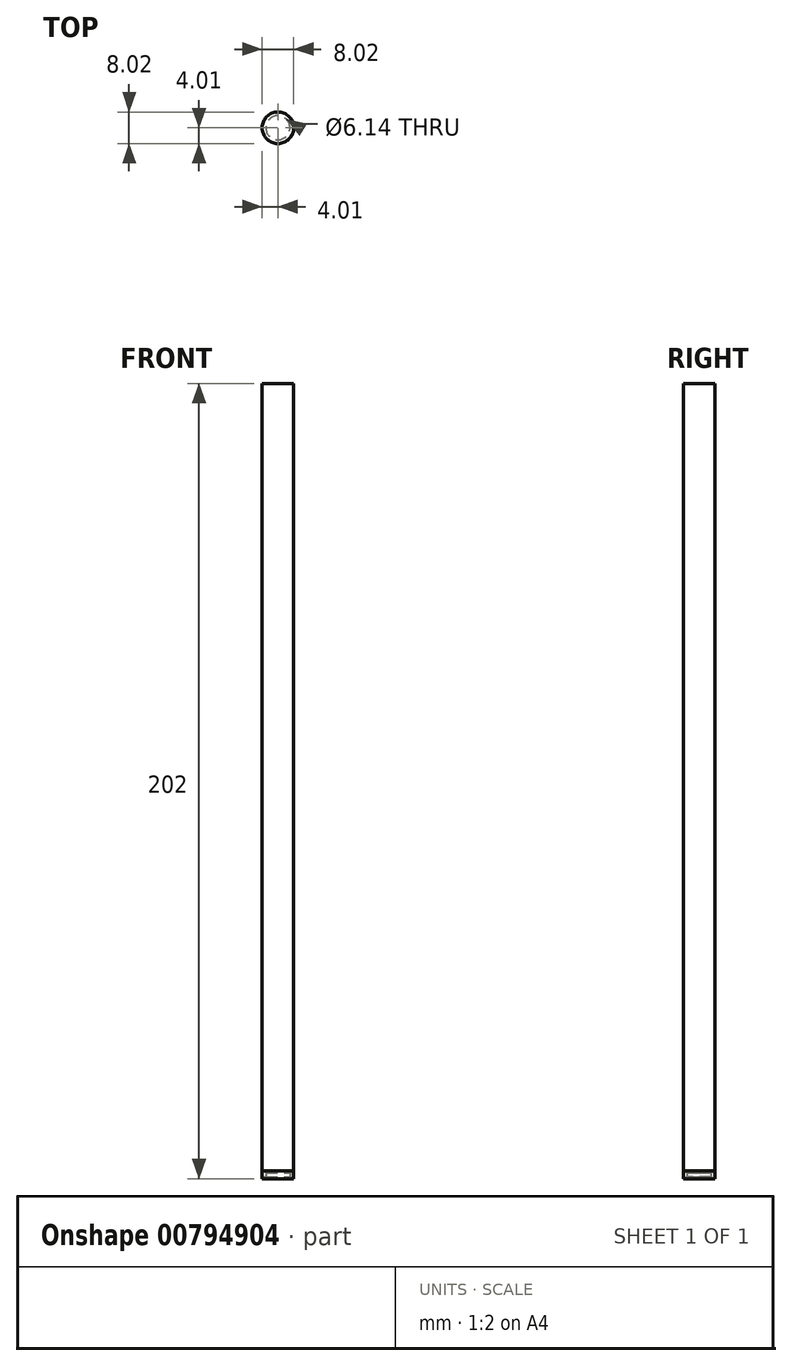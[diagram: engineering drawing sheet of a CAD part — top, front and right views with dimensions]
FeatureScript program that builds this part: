
annotation { "Feature Type Name" : "Feature", "Feature Type Description" : "" }
export const myFeature = defineFeature(function(context is Context, id is Id, definition is map)
    precondition{}
    {
        {
            var Q0;
            Q0=qCreatedBy(makeId("Top.planeOp"),FACE);
            var sketch = newSketch(context, id + "F0", { "sketchPlane" : qUnion([Q0])});
            skCircle(sketch, "E0", {"center": v(0, 0) * mm, "radius": 4 * mm});
            skSolve(sketch);
        }
        {
            var Q0;
            Q0=makeQuery(id+"F0.imprint","IMPRINT",FACE,{"disambiguationData":[TD([[makeQuery(id+"F0.imprint","IMPRINT",EDGE,{"derivedFrom":sQuery(id+"F0.wireOp",EDGE,"E0")}),1.0]])]});
            extrude(context, id + "F1", {"entities" : qUnion([Q0]), "depth" : 200 * mm, "offsetDistance" : 25.4 * mm});
        }
        {
            var Q0;
            Q0=qCreatedBy(makeId("Right.planeOp"),FACE);
            var sketch = newSketch(context, id + "F2", { "sketchPlane" : qUnion([Q0])});
            skLineSegment(sketch, "E1", {"start": v(-4.01, 0) * mm, "end": v(-3.07, -0.5) * mm});
            skLineSegment(sketch, "E2", {"start": v(-3.07, -0.5) * mm, "end": v(-3.07, -1.5) * mm});
            skLineSegment(sketch, "E3", {"start": v(-3.07, -1.5) * mm, "end": v(-4.01, -2) * mm});
            skLineSegment(sketch, "E4", {"start": v(-4.01, -2) * mm, "end": v(-4.01, 0) * mm});
            skSolve(sketch);
        }
        {
            var Q0;
            Q0=makeQuery(id+"F2.imprint","IMPRINT",FACE,{"disambiguationData":[TD([[makeQuery(id+"F2.imprint","IMPRINT",EDGE,{"derivedFrom":sQuery(id+"F2.wireOp",EDGE,"E1")}),-1.0]])]});
            var Q1;
            Q1=makeQuery(id+"F1.opExtrude","CAP_EDGE",EDGE,{"disambiguationData":[OSD([sQuery(id+"F0.wireOp",EDGE,"E0")])],"isStart":true});
            revolve(context, id + "F3", {"surfaceOperationType" : NewSurfaceOperationType.NEW, "entities" : qUnion([Q0]), "axis" : qUnion([Q1]), "revolveType" : RevolveType.FULL});
        }
    });
